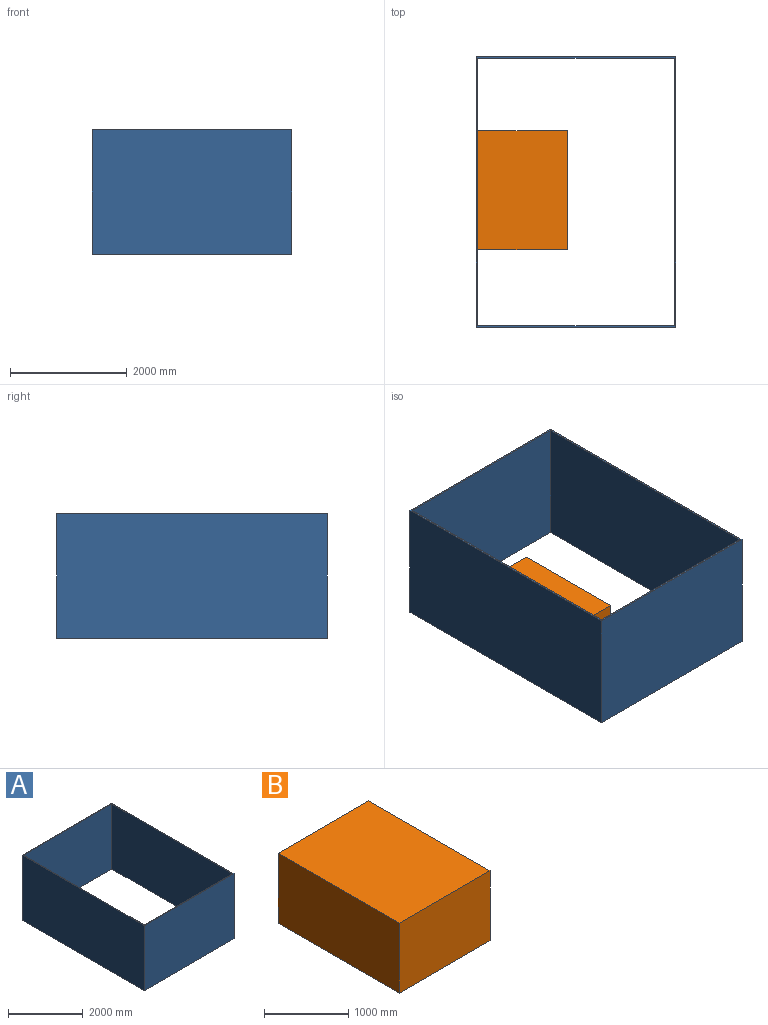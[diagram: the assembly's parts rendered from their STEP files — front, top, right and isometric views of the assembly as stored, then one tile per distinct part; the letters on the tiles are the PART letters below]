
ASSEMBLY  parts=2 mates=2
PART A: 10 faces, bbox 3403.6x4622.8x2133.6 mm
  f0: plane 3352.8x2133.6mm, normal (0,1,0), area 7153534.1mm2, adj f1,f7,f8,f9
  f1: plane 4572x2133.6mm, normal (1,0,0), area 9754819.2mm2, adj f0,f2,f8,f9
  f2: plane 3352.8x2133.6mm, normal (0,-1,0), area 7153534.1mm2, adj f1,f7,f8,f9
  f3: plane 4622.8x2133.6mm, normal (-1,0,0), area 9863206.1mm2, adj f4,f6,f8,f9
  f4: plane 3403.6x2133.6mm, normal (0,-1,0), area 7261921mm2, adj f3,f5,f8,f9
  f5: plane 4622.8x2133.6mm, normal (1,0,0), area 9863206.1mm2, adj f4,f6,f8,f9
  f6: plane 3403.6x2133.6mm, normal (0,1,0), area 7261921mm2, adj f3,f5,f8,f9
  f7: plane 4572x2133.6mm, normal (-1,0,0), area 9754819.2mm2, adj f0,f2,f8,f9
  f8: plane 4622.8x3403.6mm, normal (0,0,1), area 405160.5mm2, adj f0,f1,f2,f3,f4,f5,f6,f7
  f9: plane 4622.8x3403.6mm, normal (0,0,-1), area 405160.5mm2, adj f0,f1,f2,f3,f4,f5,f6,f7
PART B: 6 faces, bbox 1524x2032x1016 mm
  f0: plane 2032x1016mm, normal (-1,0,0), area 2064512mm2, adj f1,f3,f4,f5
  f1: plane 1524x1016mm, normal (0,-1,0), area 1548384mm2, adj f0,f2,f4,f5
  f2: plane 2032x1016mm, normal (1,0,0), area 2064512mm2, adj f1,f3,f4,f5
  f3: plane 1524x1016mm, normal (0,1,0), area 1548384mm2, adj f0,f2,f4,f5
  f4: plane 2032x1524mm, normal (0,0,1), area 3096768mm2, adj f0,f1,f2,f3
  f5: plane 2032x1524mm, normal (0,0,-1), area 3096768mm2, adj f0,f1,f2,f3
PLACE A t=(509.11,436.95,-206.28)mm fixed
PLACE B t=(-405.29,469.66,-206.28)mm
MATE planar A.f9 <-> B.f5  axis (0,0,-1) through (509.11,436.95,-206.28)mm
MATE planar A.f1 <-> B.f0  axis (1,0,0) through (-1167.29,436.95,860.52)mm
